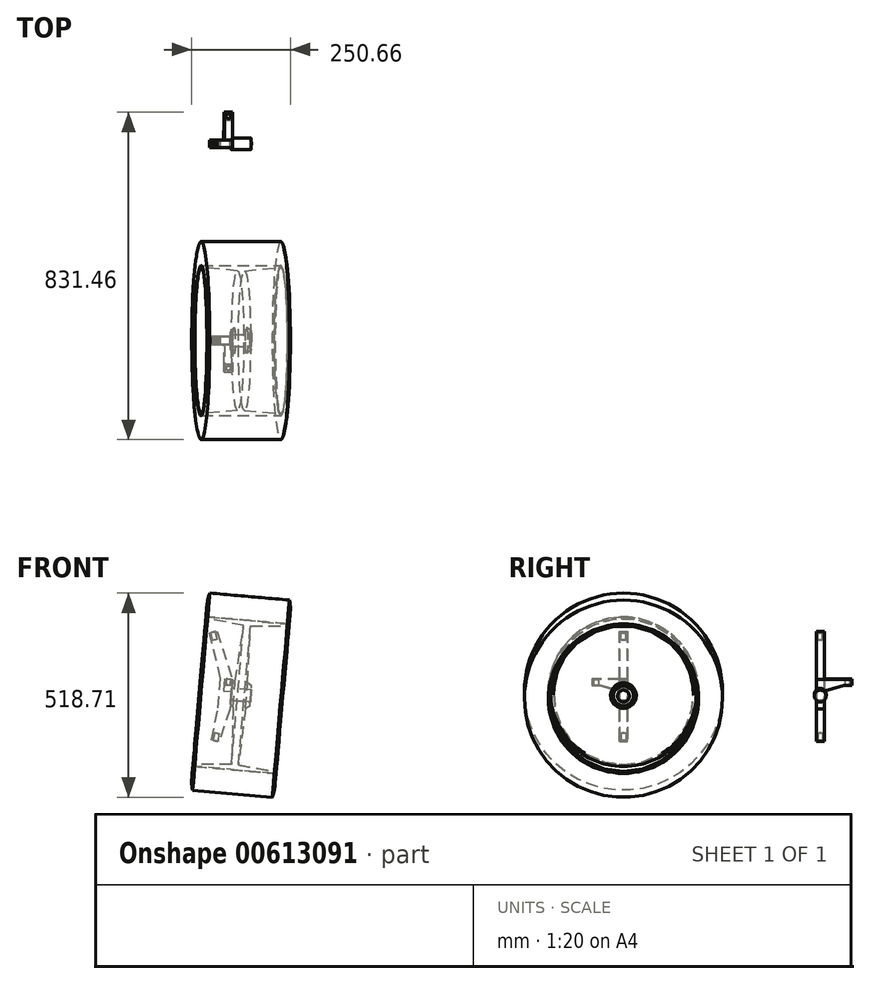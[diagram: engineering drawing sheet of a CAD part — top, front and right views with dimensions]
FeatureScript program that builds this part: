
annotation { "Feature Type Name" : "Feature", "Feature Type Description" : "" }
export const myFeature = defineFeature(function(context is Context, id is Id, definition is map)
    precondition{}
    {
        {
            var Q0;
            Q0=qCreatedBy(makeId("Front.planeOp"),FACE);
            var sketch = newSketch(context, id + "F0", { "sketchPlane" : qUnion([Q0])});
            skLineSegment(sketch, "E0", {"start": v(0, 195.2) * mm, "end": v(0, -200.25) * mm, "construction": true});
            skLineSegment(sketch, "E1", {"start": v(22.1, 171.93) * mm, "end": v(61.54, 49) * mm});
            skLineSegment(sketch, "E2", {"start": v(61.54, 49) * mm, "end": v(55, -25.72) * mm});
            skLineSegment(sketch, "E3", {"start": v(55, -25.72) * mm, "end": v(27.69, -108.53) * mm});
            skLineSegment(sketch, "E4", {"start": v(27.69, -108.53) * mm, "end": v(8.1, -104.44) * mm});
            skLineSegment(sketch, "E5", {"start": v(8.1, -104.44) * mm, "end": v(25.12, -23.1) * mm});
            skLineSegment(sketch, "E6", {"start": v(25.12, -23.1) * mm, "end": v(31.66, 51.6) * mm});
            skLineSegment(sketch, "E7", {"start": v(31.66, 51.6) * mm, "end": v(2.7, 167.07) * mm});
            skLineSegment(sketch, "E8", {"start": v(2.7, 167.07) * mm, "end": v(22.1, 171.93) * mm});
            skLineSegment(sketch, "E9", {"start": v(77.72, 233.86) * mm, "end": v(1.17, -641.1) * mm, "construction": true});
            skLineSegment(sketch, "E10", {"start": v(61.54, 49) * mm, "end": v(-208.12, 72.58) * mm, "construction": true});
            skLineSegment(sketch, "E11", {"start": v(55, -25.72) * mm, "end": v(-212.03, -2.36) * mm, "construction": true});
            skLineSegment(sketch, "E12", {"start": v(141.06, 4.4) * mm, "end": v(-205.15, 34.68) * mm, "construction": true});
            skSolve(sketch);
        }
        {
            var Q0;
            Q0=qSketchRegion(id+"F0",true);
            extrude(context, id + "F1", {"entities" : qUnion([Q0]), "endBound" : BoundingType.SYMMETRIC, "depth" : 20 * mm});
        }
        {
            var Q0;
            Q0=makeQuery(id+"F1.opExtrude","SWEPT_FACE",FACE,{"disambiguationData":[OSD([sQuery(id+"F0.wireOp",EDGE,"E2")])]});
            var sketch = newSketch(context, id + "F2", { "sketchPlane" : qUnion([Q0])});
            skCircle(sketch, "E13", {"center": v(0, 16.67) * mm, "radius": 15 * mm});
            skLineSegment(sketch, "E14", {"start": v(-21.08, 16.67) * mm, "end": v(59.96, 16.67) * mm, "construction": true});
            skPoint(sketch, "E14.startSnap0", {"position": v(-10, 16.67) * mm});
            skSolve(sketch);
        }
        {
            var Q0;
            Q0=qSketchRegion(id+"F2",true);
            extrude(context, id + "F3", {"entities" : qUnion([Q0]), "operationType" : NewBodyOperationType.ADD, "depth" : 50 * mm});
        }
        {
            var Q0;
            Q0=makeQuery(id+"F1.opExtrude","SWEPT_BODY",BODY,{"disambiguationData":[OSD([sQuery(id+"F0.wireOp",EDGE,"E1"),sQuery(id+"F0.wireOp",EDGE,"E2"),sQuery(id+"F0.wireOp",EDGE,"E3"),sQuery(id+"F0.wireOp",EDGE,"E4"),sQuery(id+"F0.wireOp",EDGE,"E5"),sQuery(id+"F0.wireOp",EDGE,"E6"),sQuery(id+"F0.wireOp",EDGE,"E7"),sQuery(id+"F0.wireOp",EDGE,"E8")])]});
            transform(context, id + "F4", {"entities" : qUnion([Q0]), "transformType" : TransformType.TRANSLATION_3D, "dx" : 0 * mm, "dy" : 500 * mm, "dz" : 0 * mm, "makeCopy" : true});
        }
        {
            var Q0;
            Q0=makeQuery(id+"F1.opExtrude","SWEPT_FACE",FACE,{"disambiguationData":[OSD([sQuery(id+"F0.wireOp",EDGE,"E2")])]});
            var sketch = newSketch(context, id + "F5", { "sketchPlane" : qUnion([Q0])});
            skLineSegment(sketch, "E15", {"start": v(-10, 54.17) * mm, "end": v(-80, 54.17) * mm});
            skLineSegment(sketch, "E16", {"start": v(-80, 54.17) * mm, "end": v(-80, 39.17) * mm});
            skLineSegment(sketch, "E17", {"start": v(-80, 39.17) * mm, "end": v(-60, 39.17) * mm});
            skLineSegment(sketch, "E18", {"start": v(-60, 39.17) * mm, "end": v(-10, 24.17) * mm});
            skLineSegment(sketch, "E19", {"start": v(-10, 54.17) * mm, "end": v(-10, 24.17) * mm});
            skSolve(sketch);
        }
        {
            var Q0;
            {var subQ1=sQuery(id+"F5.wireOp",EDGE,"E15");Q0=makeQuery(id+"F5.imprint","IMPRINT",FACE,{"disambiguationData":[TD([[makeQuery(id+"F5.imprint","IMPRINT",EDGE,{"derivedFrom":subQ1}),1.0]])]});}
            extrude(context, id + "F6", {"entities" : qUnion([Q0]), "operationType" : NewBodyOperationType.ADD, "oppositeDirection" : true, "depth" : 20 * mm});
        }
        {
            var Q0;
            Q0=makeQuery(id+"F6.opExtrude","SWEPT_FACE",FACE,{"disambiguationData":[OSD([sQuery(id+"F5.wireOp",EDGE,"E17")])]});
            var sketch = newSketch(context, id + "F7", { "sketchPlane" : qUnion([Q0])});
            skLineSegment(sketch, "E20", {"start": v(47.04, 54.98) * mm, "end": v(47.04, 93.52) * mm, "construction": true});
            skPoint(sketch, "E20.startSnap0", {"position": v(47.04, 60) * mm});
            skPoint(sketch, "E20.endSnap0", {"position": v(47.04, 80) * mm});
            skLineSegment(sketch, "E21", {"start": v(30.33, 70) * mm, "end": v(69.98, 70) * mm, "construction": true});
            skPoint(sketch, "E21.startSnap0", {"position": v(37.04, 70) * mm});
            skCircle(sketch, "E22", {"center": v(47.04, 70) * mm, "radius": 6 * mm});
            skSolve(sketch);
        }
        {
            var Q0;
            Q0=qSketchRegion(id+"F7",true);
            extrude(context, id + "F8", {"entities" : qUnion([Q0]), "operationType" : NewBodyOperationType.REMOVE, "endBound" : BoundingType.THROUGH_ALL, "oppositeDirection" : true, "depth" : 25 * mm});
        }
        {
            var Q0;
            Q0=makeQuery(id+"F1.opExtrude","SWEPT_FACE",FACE,{"disambiguationData":[OSD([sQuery(id+"F0.wireOp",EDGE,"E8")])]});
            var sketch = newSketch(context, id + "F9", { "sketchPlane" : qUnion([Q0])});
            skLineSegment(sketch, "E23", {"start": v(23.73, 0) * mm, "end": v(-73.3, 0) * mm, "construction": true});
            skPoint(sketch, "E23.endSnap0", {"position": v(63.26, 0) * mm});
            skLineSegment(sketch, "E24", {"start": v(53.26, -38.65) * mm, "end": v(53.26, 35.78) * mm, "construction": true});
            skPoint(sketch, "E24.startSnap0", {"position": v(53.26, -10) * mm});
            skCircle(sketch, "E25", {"center": v(53.26, 0) * mm, "radius": 6 * mm});
            skSolve(sketch);
        }
        {
            var Q0;
            Q0=qSketchRegion(id+"F9",true);
            extrude(context, id + "F10", {"entities" : qUnion([Q0]), "operationType" : NewBodyOperationType.REMOVE, "oppositeDirection" : true, "depth" : 20 * mm});
        }
        {
            var Q0;
            Q0=makeQuery(id+"F1.opExtrude","SWEPT_FACE",FACE,{"disambiguationData":[OSD([sQuery(id+"F0.wireOp",EDGE,"E4")])]});
            var sketch = newSketch(context, id + "F11", { "sketchPlane" : qUnion([Q0])});
            skLineSegment(sketch, "E26", {"start": v(-17, 0) * mm, "end": v(100.49, 0) * mm, "construction": true});
            skLineSegment(sketch, "E27", {"start": v(39.32, -28.2) * mm, "end": v(39.32, 57.2) * mm, "construction": true});
            skPoint(sketch, "E27.startSnap0", {"position": v(39.32, -10) * mm});
            skCircle(sketch, "E28", {"center": v(39.32, 0) * mm, "radius": 6 * mm});
            skSolve(sketch);
        }
        {
            var Q0;
            Q0=qSketchRegion(id+"F11",true);
            extrude(context, id + "F12", {"entities" : qUnion([Q0]), "operationType" : NewBodyOperationType.REMOVE, "oppositeDirection" : true, "depth" : 20 * mm});
        }
        {
            var Q0;
            Q0=qCreatedBy(makeId("Front.planeOp"),FACE);
            var sketch = newSketch(context, id + "F13", { "sketchPlane" : qUnion([Q0])});
            skLineSegment(sketch, "E29", {"start": v(59.58, 26.58) * mm, "end": v(110.33, 22.14) * mm, "construction": true});
            skLineSegment(sketch, "E30.0", {"start": v(109.4, 22.22) * mm, "end": v(106.78, -7.67) * mm, "construction": true});
            skLineSegment(sketch, "E31", {"start": v(240.38, -4.3) * mm, "end": v(-99.22, 25.41) * mm, "construction": true});
            skLineSegment(sketch, "E32", {"start": v(59.58, 26.58) * mm, "end": v(60.52, 37.3) * mm});
            skLineSegment(sketch, "E33", {"start": v(110.33, 32.94) * mm, "end": v(109.4, 22.22) * mm});
            skLineSegment(sketch, "E34", {"start": v(-35.82, 211.1) * mm, "end": v(269.76, 184.36) * mm, "construction": true});
            skLineSegment(sketch, "E35", {"start": v(-1.43, 208.08) * mm, "end": v(201, 190.37) * mm});
            skLineSegment(sketch, "E36", {"start": v(-1.43, 208.08) * mm, "end": v(-1.87, 203.1) * mm});
            skLineSegment(sketch, "E37", {"start": v(-1.87, 203.1) * mm, "end": v(89.96, 186.91) * mm});
            skLineSegment(sketch, "E38", {"start": v(89.96, 186.91) * mm, "end": v(68.54, 43.85) * mm});
            skLineSegment(sketch, "E39", {"start": v(68.54, 43.85) * mm, "end": v(60.52, 37.3) * mm});
            skLineSegment(sketch, "E40", {"start": v(201, 190.37) * mm, "end": v(200.56, 185.4) * mm});
            skLineSegment(sketch, "E41", {"start": v(200.56, 185.4) * mm, "end": v(107.32, 185.4) * mm});
            skLineSegment(sketch, "E42", {"start": v(107.32, 185.4) * mm, "end": v(100.16, 40.92) * mm});
            skLineSegment(sketch, "E43", {"start": v(100.16, 40.92) * mm, "end": v(110.33, 32.94) * mm});
            skLineSegment(sketch, "E44", {"start": v(59.58, 26.58) * mm, "end": v(110.33, 22.14) * mm});
            skLineSegment(sketch, "E45", {"start": v(106.78, -7.67) * mm, "end": v(56.97, -3.3) * mm, "construction": true});
            skLineSegment(sketch, "E46", {"start": v(77.43, -56.23) * mm, "end": v(106.55, 276.61) * mm, "construction": true});
            skSolve(sketch);
        }
        {
            var Q0;
            Q0=qSketchRegion(id+"F13",true);
            var Q1;
            Q1=makeQuery(id+"F3.opExtrude","SWEPT_FACE",FACE,{"disambiguationData":[OSD([sQuery(id+"F2.wireOp",EDGE,"E13")])]});
            revolve(context, id + "F14", {"entities" : qUnion([Q0]), "axis" : qUnion([Q1]), "revolveType" : RevolveType.FULL});
        }
        {
            var Q0;
            Q0=qCreatedBy(makeId("Front.planeOp"),FACE);
            var sketch = newSketch(context, id + "F15", { "sketchPlane" : qUnion([Q0])});
            skLineSegment(sketch, "E47", {"start": v(-1.43, 208.08) * mm, "end": v(201, 190.37) * mm, "construction": true});
            skLineSegment(sketch, "E48.0", {"start": v(-1.43, 208.08) * mm, "end": v(-34.64, -171.47) * mm, "construction": true});
            skLineSegment(sketch, "E49.0", {"start": v(201, 190.37) * mm, "end": v(167.79, -189.18) * mm, "construction": true});
            skLineSegment(sketch, "E50", {"start": v(3.88, 268.81) * mm, "end": v(206.3, 251.1) * mm});
            skLineSegment(sketch, "E51", {"start": v(116.7, 392.7) * mm, "end": v(90.07, 88.2) * mm, "construction": true});
            skLineSegment(sketch, "E52", {"start": v(21.36, 236.69) * mm, "end": v(295, 212.75) * mm, "construction": true});
            skArc(sketch, "E53", {"start": v(3.88, 268.81) * mm, "mid": v(-3.23, 238.84) * mm, "end": v(-1.43, 208.08) * mm});
            skArc(sketch, "E54", {"start": v(206.3, 251.1) * mm, "mid": v(208.1, 220.35) * mm, "end": v(201, 190.37) * mm});
            skLineSegment(sketch, "E55", {"start": v(-1.43, 208.08) * mm, "end": v(201, 190.37) * mm});
            skSolve(sketch);
        }
        {
            var Q0;
            Q0=qSketchRegion(id+"F15",true);
            var Q1;
            Q1=makeQuery(id+"F14.opRevolve","SWEPT_FACE",FACE,{"disambiguationData":[OSD([sQuery(id+"F13.wireOp",EDGE,"E35")])]});
            revolve(context, id + "F16", {"entities" : qUnion([Q0]), "axis" : qUnion([Q1]), "revolveType" : RevolveType.FULL});
        }
        {
            var Q0;
            {var subQ6=sQuery(id+"F0.wireOp",EDGE,"E2");var subQ7=sQuery(id+"F0.wireOp",EDGE,"E1");Q0=makeQuery(id+"F4.opPattern","COPY",FACE,{"derivedFrom":makeQuery(id+"F3.boolean.opBoolean","SPLIT",FACE,{"disambiguationData":[TD([makeQuery(id+"F1.opExtrude","SWEPT_FACE",FACE,{"disambiguationData":[OSD([subQ7])]})])],"derivedFrom":makeQuery(id+"F1.opExtrude","SWEPT_FACE",FACE,{"disambiguationData":[OSD([subQ6])]})}),"instanceName":"1"});}
            var sketch = newSketch(context, id + "F17", { "sketchPlane" : qUnion([Q0])});
            skLineSegment(sketch, "E56", {"start": v(510, 54.17) * mm, "end": v(580, 54.17) * mm});
            skLineSegment(sketch, "E57", {"start": v(580, 54.17) * mm, "end": v(580, 39.17) * mm});
            skLineSegment(sketch, "E58", {"start": v(580, 39.17) * mm, "end": v(560, 39.17) * mm});
            skLineSegment(sketch, "E59", {"start": v(560, 39.17) * mm, "end": v(510, 24.17) * mm});
            skLineSegment(sketch, "E60", {"start": v(510, 24.17) * mm, "end": v(510, 54.17) * mm});
            skSolve(sketch);
        }
        {
            var Q0;
            Q0=qSketchRegion(id+"F17",true);
            extrude(context, id + "F18", {"entities" : qUnion([Q0]), "operationType" : NewBodyOperationType.ADD, "oppositeDirection" : true, "depth" : 20 * mm});
        }
        {
            var Q0;
            Q0=makeQuery(id+"F18.opExtrude","SWEPT_FACE",FACE,{"disambiguationData":[OSD([sQuery(id+"F17.wireOp",EDGE,"E56")])]});
            var sketch = newSketch(context, id + "F19", { "sketchPlane" : qUnion([Q0])});
            skCircle(sketch, "E61", {"center": v(47.04, 570) * mm, "radius": 6 * mm});
            skSolve(sketch);
        }
        {
            var Q0;
            Q0=qSketchRegion(id+"F19",true);
            extrude(context, id + "F20", {"entities" : qUnion([Q0]), "operationType" : NewBodyOperationType.REMOVE, "endBound" : BoundingType.THROUGH_ALL, "oppositeDirection" : true, "depth" : 25 * mm});
        }
        {
            var Q0;
            Q0=makeQuery(id+"F4.opPattern","COPY",FACE,{"derivedFrom":makeQuery(id+"F1.opExtrude","SWEPT_FACE",FACE,{"disambiguationData":[OSD([sQuery(id+"F0.wireOp",EDGE,"E8")])]}),"instanceName":"1"});
            var sketch = newSketch(context, id + "F21", { "sketchPlane" : qUnion([Q0])});
            skCircle(sketch, "E62", {"center": v(53.26, 500) * mm, "radius": 6 * mm});
            skPoint(sketch, "E62.centerSnap0", {"position": v(53.26, 510) * mm});
            skPoint(sketch, "E62.centerSnap1", {"position": v(43.26, 500) * mm});
            skSolve(sketch);
        }
        {
            var Q0;
            Q0=qSketchRegion(id+"F21",true);
            extrude(context, id + "F22", {"entities" : qUnion([Q0]), "operationType" : NewBodyOperationType.REMOVE, "oppositeDirection" : true, "depth" : 20 * mm});
        }
        {
            var Q0;
            Q0=makeQuery(id+"F4.opPattern","COPY",FACE,{"derivedFrom":makeQuery(id+"F1.opExtrude","SWEPT_FACE",FACE,{"disambiguationData":[OSD([sQuery(id+"F0.wireOp",EDGE,"E4")])]}),"instanceName":"1"});
            var sketch = newSketch(context, id + "F23", { "sketchPlane" : qUnion([Q0])});
            skCircle(sketch, "E63", {"center": v(39.32, -500) * mm, "radius": 6 * mm});
            skPoint(sketch, "E63.centerSnap0", {"position": v(39.32, -510) * mm});
            skPoint(sketch, "E63.centerSnap1", {"position": v(29.32, -500) * mm});
            skSolve(sketch);
        }
        {
            var Q0;
            Q0=qSketchRegion(id+"F23",true);
            extrude(context, id + "F24", {"entities" : qUnion([Q0]), "operationType" : NewBodyOperationType.REMOVE, "oppositeDirection" : true, "depth" : 20 * mm});
        }
    });
